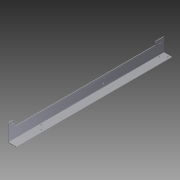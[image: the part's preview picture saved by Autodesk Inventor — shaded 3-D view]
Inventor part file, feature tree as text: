
AUTODESK INVENTOR PART (.ipt)
format: ipt  version: 2012 (Build 160160000, 160)  size: 91,648 bytes
history: native  units: in
note: dims shown in document units (in); Inventor stores cm internally (conversion verified against a paired STEP export)
features: other x3, sketch x1
ambient origin geometry x8: Origin, YZ Plane, XZ Plane, XY Plane, X Axis, Y Axis, Z Axis, Center Point
bodies: Solid1 (feature_tree)
feature tree (4):
  other  "8 ball top roller L frame.ipt"
  other  "Solid1::8 ball top roller L frame.ipt"
  sketch  "Sketch1"  dims[d0=0.3937in]
  other  "TaggingFeature1"
